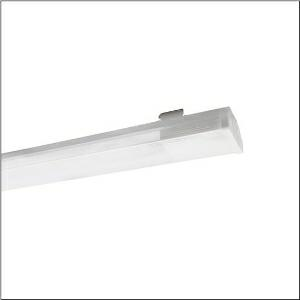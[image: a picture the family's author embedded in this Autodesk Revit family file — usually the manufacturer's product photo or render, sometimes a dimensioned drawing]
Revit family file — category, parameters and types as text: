
# Revit family: modario_31_gen_2_53bm812du4m1d2_653a
name_source: partatom
category: Lighting Fixtures
units: mm (PartAtom-declared; Revit-internal decimal feet)

## family parameters
Cut with Voids When Loaded = No
Host = Face
Light Source = No
Part Type = Normal
Room Calculation Point = No
Round Connector Dimension = Use Diameter
Shared = No

## types (1)
- --- (1 x LED, 26560 lm, 146.1 W, 4000K)
    Apparent Load = 146 VA
    CIE Flux Codes = 47 80 95 93 100
    Color Rendering = 80
    Color Temperature = 4000K
    Default Elevation = 1800 mm
    Description = Modario 31 Gen.2, luminaire insert, of sheet steel, coil coated, white, length: 2.392mm, width: 81mm, height: 82mm, 8x system unit, system units: 299mm, LED rated luminous flux: 26.560lm, light colour: 840, SDCM (Standard Deviation of Colour Matching)MacAdam ≤ 3 SDCM (initial), control gear: DALI 2, control gear: ECG DALI, with plug, 5-pole, with phase selection, mains connection: 220..240V, AC, 50/60Hz, rated input power: 146W, through-wiring accessed according to module size, primary optical cover: cover, of PMMA, light emission: direct distribution, primary light characteristic: symmetric, protection rating (complete): IP20, protection rating (LED compartment): IP50, insulation class (complete): insulation class I (protective earthing), certification: CE, ENEC, VDE, UKCA, impact resistance: IK03, permissible ambient temperature for indoor applications: -40..+30°C, corresponds to IFS (International Featured Standards) requirements for safety and quality in the food industry, reducing of maximum allowable ambient temperature of 5°C with ceiling mounting, IP40 when using the optional accessory 5TP9018, packaging unit: 1 piece
    Height = 92 mm
    Lamp = 1 x LED
    Lamp Light Flux = 26560 lm
    Lamp Power = 146.1 W
    Lamp count = 1
    Length = 2392 mm
    Luminous efficacy = 182 lm/W
    Manufacturer = Siteco
    ModVariant = No
    Model = 53BM812DU4M1D2
    Mounting Place = Ceiling
    Mounting Type = Pendant
    Number of Poles = 1
    OnlyDefault = Yes
    Power Factor = 1
    Product Name = Modario 31 Gen.2
    Product group = luminaire insert | ceiling pendant
    ProductGroupID = 901
    Protection Class = Protection class I
    Protection Degree = IP 20
    RLX_Detail_Level = 1
    RLX_Emergency_Light_Flux = 0 lm
    RLX_Emergency_Type = 0
    RLX_Emergency_Type_DB = No
    RlxData = <blob elided: 38545 chars, md5=c25c3167>
    Socket = socket
    Standby Power = 0 W
    System Light Flux = 26560 lm
    System Power = 146 W
    Type Comments = factory setting: luminous flux: 100 % | dim-lin: 254 | 676 mA
    Type Image = l_1341883.jpg
    URL = http://relux.com
    VarID = @adj_050851
    Voltage = 0 V
    Weight = 0.00 kg
    Width = 81 mm

## geometry (parser evidence)
native form markers: Blend x4, Sweep x14
no freeform markers — native parametric forms only
